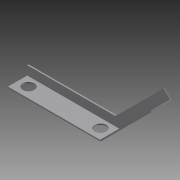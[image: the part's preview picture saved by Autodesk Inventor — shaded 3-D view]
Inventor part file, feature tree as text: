
AUTODESK INVENTOR PART (.ipt)
format: ipt  version: 2012 (Build 160160000, 160)  size: 107,008 bytes
history: native  units: in
note: dims shown in document units (in); Inventor stores cm internally (conversion verified against a paired STEP export)
features: extrude x3, sketch x2
ambient origin geometry x8: Origin, YZ Plane, XZ Plane, XY Plane, X Axis, Y Axis, Z Axis, Center Point
bodies: Solid1 (feature_tree)
feature tree (5):
  sketch  "Sketch1"  dims[d4=0.125in d6=0.125in]
  extrude  "Extrusion1"  Depth=0.125in
  extrude  "Extrusion2"  Depth=1.0in
  extrude  "Extrusion3"  TaperAngle=45.0deg  [1 undecoded]
  sketch  "Sketch2"  dims[d8=1.0in d9=1.0in d10=45.0deg d11=9.0in d12=7.0in d13=0.0625in d14=0.125in d15=0.0in d16=2.0in d17=0.0in d18=1.125in d19=1.0in d20=1.0in d21=1.0in d22=1.0in d23=0.0in]
note: 1 required parameter value undecoded (feature->parameter linkage not recoverable at this tier; creation-order binding heuristic only, values carry confidence <= 0.55)
